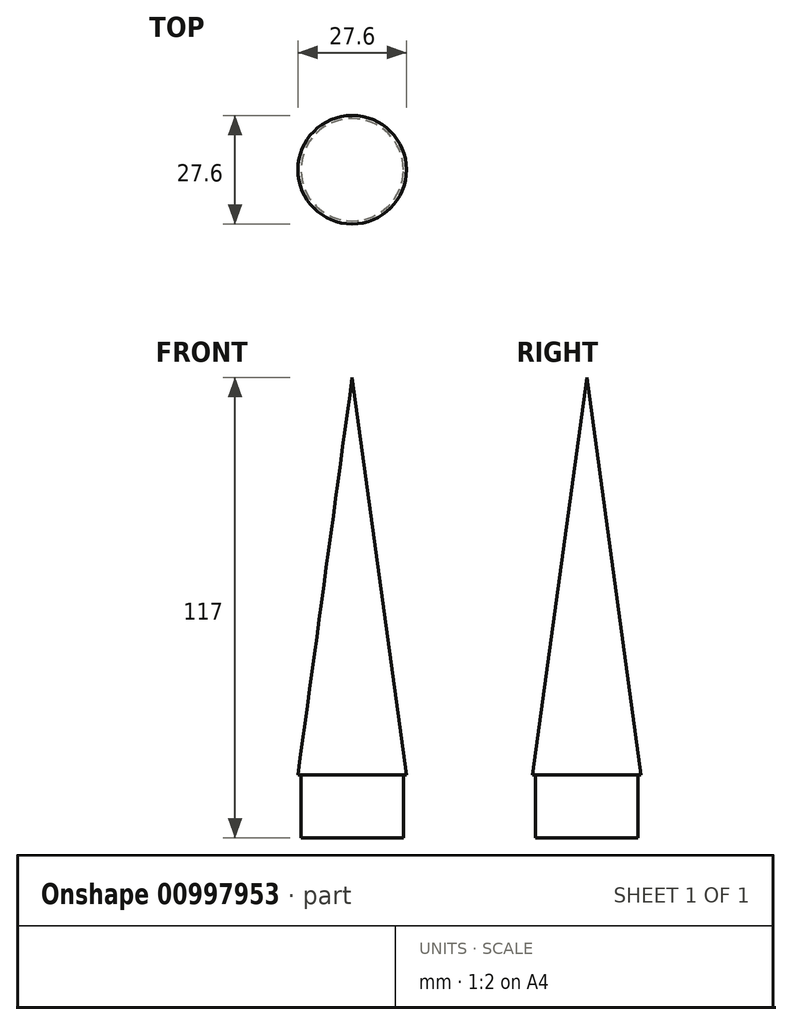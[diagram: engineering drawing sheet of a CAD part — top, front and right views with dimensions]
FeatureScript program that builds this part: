
annotation { "Feature Type Name" : "Feature", "Feature Type Description" : "" }
export const myFeature = defineFeature(function(context is Context, id is Id, definition is map)
    precondition{}
    {
        {
            var Q0;
            Q0=qCreatedBy(makeId("Front.planeOp"),FACE);
            var sketch = newSketch(context, id + "F0", { "sketchPlane" : qUnion([Q0])});
            skLineSegment(sketch, "E0", {"start": v(0, 0) * mm, "end": v(13, 0) * mm});
            skLineSegment(sketch, "E1", {"start": v(13, 0) * mm, "end": v(13, 16) * mm});
            skLineSegment(sketch, "E2", {"start": v(13, 16) * mm, "end": v(13.8, 16) * mm});
            skLineSegment(sketch, "E3", {"start": v(13.8, 16) * mm, "end": v(0, 117) * mm});
            skLineSegment(sketch, "E4", {"start": v(0, 117) * mm, "end": v(0, 0) * mm});
            skSolve(sketch);
        }
        {
            var Q0;
            Q0=makeQuery(id+"F0.imprint","IMPRINT",FACE,{"disambiguationData":[TD([[makeQuery(id+"F0.imprint","IMPRINT",EDGE,{"derivedFrom":sQuery(id+"F0.wireOp",EDGE,"E0")}),1.0]])]});
            var Q1;
            Q1=sQuery(id+"F0.wireOp",EDGE,"E4");
            revolve(context, id + "F1", {"surfaceOperationType" : NewSurfaceOperationType.NEW, "entities" : qUnion([Q0]), "axis" : qUnion([Q1]), "revolveType" : RevolveType.FULL});
        }
    });
